# Revit family: Valvula de control con detector de flujo
name_source: partatom
category: Accesorios de tuberías
revit_build: Autodesk Revit 2017 (Build: 20160225_1515(x64)
units: mm (PartAtom-declared; Revit-internal decimal feet)

## family parameters
Compartido = No
Corte con vacíos al cargar = No
Cota de conector redondo = Radio de uso
Número OmniClass = 23.65.55.14.17
Se basa en plano de trabajo = No
Siempre vertical = Sí
Tipo de pieza = Válvula - Se divide en
Título OmniClass = Adjusting/Controlling Valves for Liquid Services

## types (1)
- Válvula de control con detector de flujo - D 16 mm
    A mm = 70 mm  [stored 0.229659 ft]
    D1 = 30 mm  [stored 0.0984252 ft]
    D2 = 45 mm  [stored 0.147638 ft]
    D3 = 68 mm
    D4 = 15 mm  [stored 0.0492126 ft]
    Descripción = Dispositivo de control diseñado como elemento de supervisión del sistema de agua nebulizada. Se instala en aquellos tramos de tubería en los que se precise una confirmación de estado y garantía de funcionamiento del sistema en caso de disparo. Este equipo se fabrica en acero inoxidable para cuatro diámetros de paso del colector.
    Fabricante = Grupo Aguilera
    H mm = 138 mm  [stored 0.452756 ft]
    L mm = 99 mm  [stored 0.324803 ft]
    Modelo = AN/VC16
    R1 = 15 mm  [stored 0.0492126 ft]
    R2 = 23 mm
    R3 = 34 mm
    R4 = 8 mm  [stored 0.0262467 ft]
    Radio = 8 mm  [stored 0.0262467 ft]
    Símbolo = Sí
    Símbolo texto = Sí
    URL = http://aguilera.es

note: [stored X ft] marks values corroborated as IEEE doubles in the binary element streams (Revit-internal decimal feet)

## geometry (parser evidence)
native form markers: Sweep x3
no freeform markers — native parametric forms only
